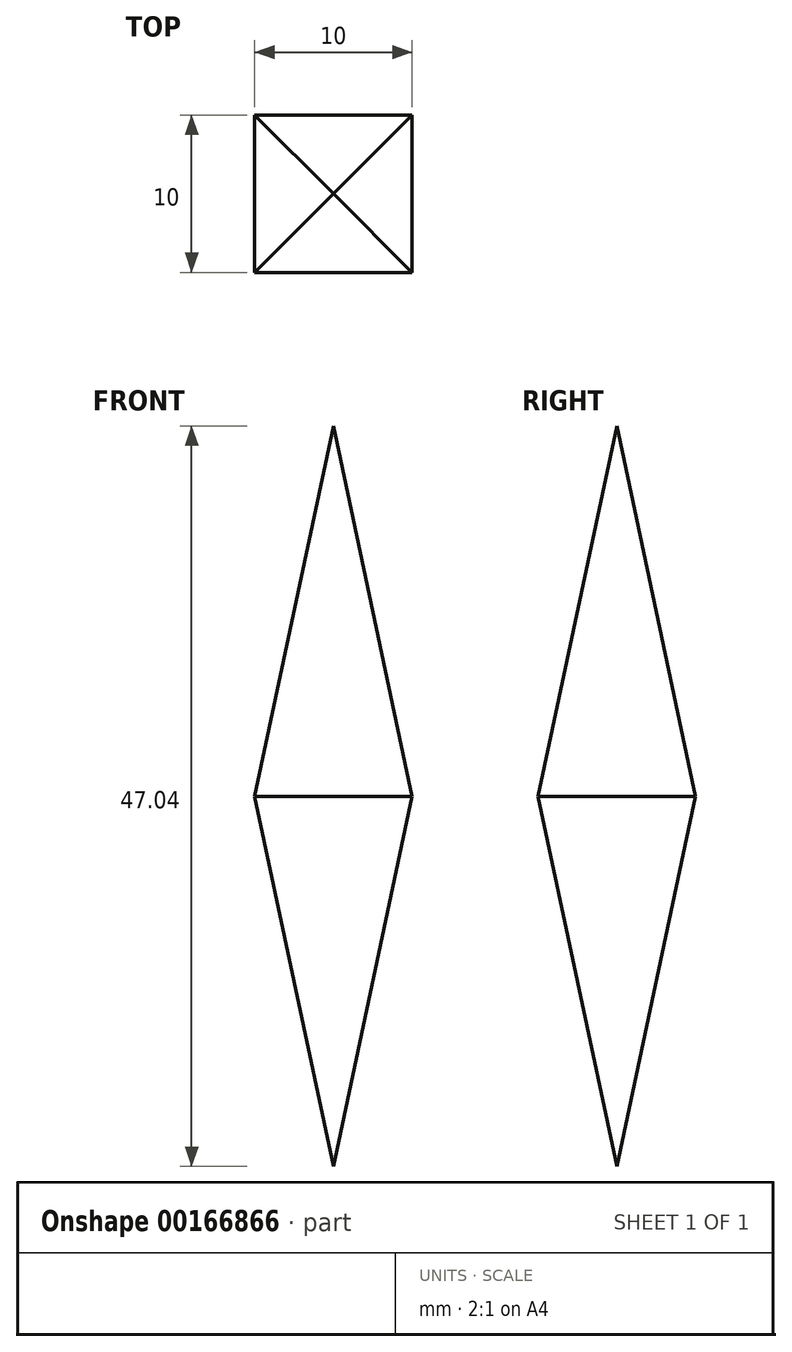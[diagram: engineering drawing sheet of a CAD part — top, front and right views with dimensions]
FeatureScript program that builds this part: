
annotation { "Feature Type Name" : "Feature", "Feature Type Description" : "" }
export const myFeature = defineFeature(function(context is Context, id is Id, definition is map)
    precondition{}
    {
        {
            var Q0;
            Q0=qCreatedBy(makeId("Top.planeOp"),FACE);
            var sketch = newSketch(context, id + "F0", { "sketchPlane" : qUnion([Q0])});
            skLineSegment(sketch, "E0.bottom", {"start": v(-5, 5) * mm, "end": v(5, 5) * mm});
            skLineSegment(sketch, "E0.top", {"start": v(-5, -5) * mm, "end": v(5, -5) * mm});
            skLineSegment(sketch, "E0.left", {"start": v(-5, 5) * mm, "end": v(-5, -5) * mm});
            skLineSegment(sketch, "E0.right", {"start": v(5, 5) * mm, "end": v(5, -5) * mm});
            skPoint(sketch, "E0.middle", {"position": v(0, 0) * mm});
            skSolve(sketch);
        }
        {
            var Q0;
            Q0=makeQuery(id+"F0.imprint","IMPRINT",FACE,{"disambiguationData":[TD([[makeQuery(id+"F0.imprint","IMPRINT",EDGE,{"derivedFrom":sQuery(id+"F0.wireOp",EDGE,"E0.bottom")}),-1.0]])]});
            extrude(context, id + "F1", {"entities" : qUnion([Q0]), "depth" : 25 * mm, "hasDraft" : true, "draftAngle" : 12 * degree, "draftPullDirection" : true, "hasSecondDirection" : true, "secondDirectionOppositeDirection" : true, "secondDirectionDepth" : 25 * mm, "hasSecondDirectionDraft" : true, "secondDirectionDraftAngle" : 12 * degree, "secondDirectionDraftPullDirection" : true});
        }
    });
